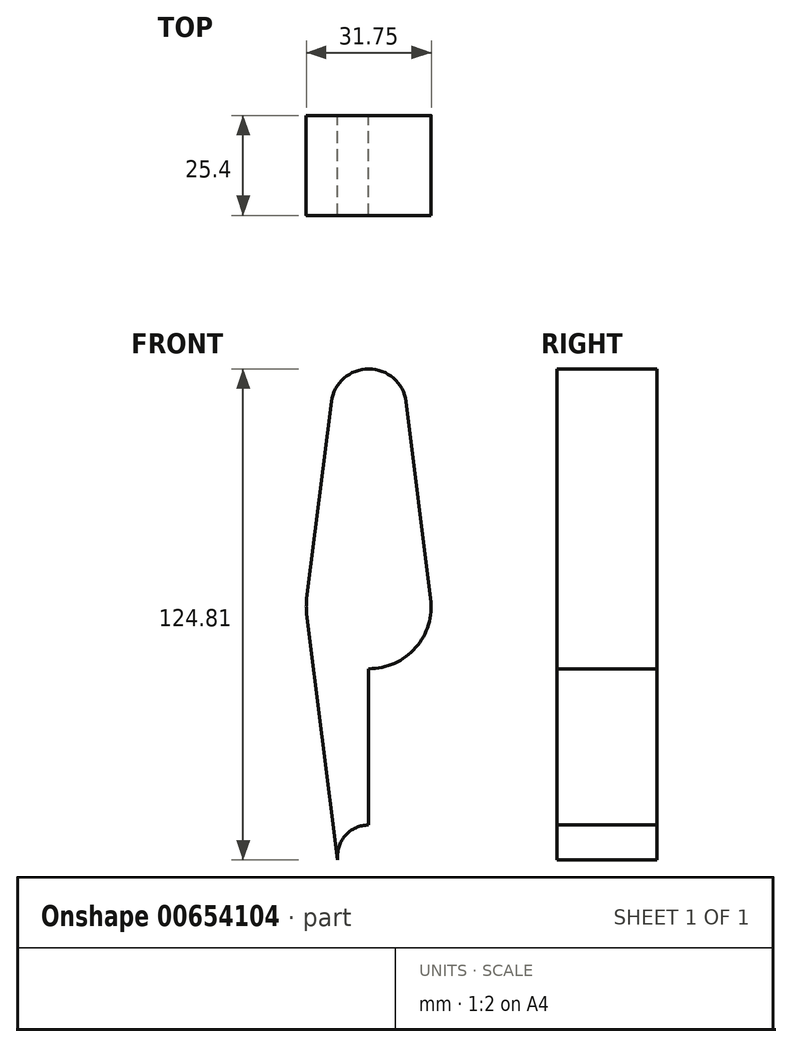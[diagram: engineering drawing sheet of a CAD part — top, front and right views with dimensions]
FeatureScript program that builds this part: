
annotation { "Feature Type Name" : "Feature", "Feature Type Description" : "" }
export const myFeature = defineFeature(function(context is Context, id is Id, definition is map)
    precondition{}
    {
        {
            var Q0;
            Q0=qCreatedBy(makeId("Front.planeOp"),FACE);
            var sketch = newSketch(context, id + "F0", { "sketchPlane" : qUnion([Q0])});
            skLineSegment(sketch, "E0", {"start": v(-10.04, 50.8) * mm, "end": v(-10.04, -63.5) * mm});
            skLineSegment(sketch, "E1", {"start": v(-10.04, -63.5) * mm, "end": v(34.41, -63.5) * mm});
            skCircle(sketch, "E2", {"center": v(-10.04, 50.8) * mm, "radius": 9.53 * mm});
            skCircle(sketch, "E3", {"center": v(-10.04, 0) * mm, "radius": 15.88 * mm});
            skPoint(sketch, "E3.centerSnap0", {"position": v(-10.04, -6.35) * mm});
            skCircle(sketch, "E4", {"center": v(-10.04, -63.5) * mm, "radius": 7.94 * mm});
            skCircle(sketch, "E5", {"center": v(34.41, -63.5) * mm, "radius": 7.94 * mm});
            skLineSegment(sketch, "E6", {"start": v(-19.49, 52) * mm, "end": v(-26.04, 0) * mm});
            skLineSegment(sketch, "E7", {"start": v(-26.04, 0) * mm, "end": v(-17.91, -64.5) * mm});
            skLineSegment(sketch, "E8", {"start": v(-0.59, 52) * mm, "end": v(5.96, 0) * mm});
            skLineSegment(sketch, "E9", {"start": v(5.96, 0) * mm, "end": v(0.89, -40.3) * mm});
            skLineSegment(sketch, "E10", {"start": v(6.91, -48.95) * mm, "end": v(34.41, -55.35) * mm});
            skLineSegment(sketch, "E11", {"start": v(-10.07, -71.44) * mm, "end": v(34.41, -71.44) * mm});
            skPoint(sketch, "E12.visualSharp", {"position": v(0, -47.34) * mm});
            skArc(sketch, "E12.filletArc", {"start": v(0.89, -40.3) * mm, "mid": v(2.24, -45.78) * mm, "end": v(6.91, -48.95) * mm});
            skSolve(sketch);
        }
        {
            var Q0;
            {var subQ0=sQuery(id+"F0.wireOp",EDGE,"E2");var subQ1=sQuery(id+"F0.wireOp",EDGE,"E0");var subQ2=makeQuery(id+"F0.imprint","INTERSECT",VERTEX,{"derivedFrom":[subQ1,subQ0]});Q0=makeQuery(id+"F0.imprint","IMPRINT",FACE,{"disambiguationData":[TD([[makeQuery(id+"F0.imprint","IMPRINT",EDGE,{"disambiguationData":[TD([[subQ2,-1.0]])],"derivedFrom":subQ1}),-1.0]])]});}
            var Q1;
            {var subQ0=sQuery(id+"F0.wireOp",EDGE,"E2");var subQ1=sQuery(id+"F0.wireOp",EDGE,"E0");var subQ2=makeQuery(id+"F0.imprint","INTERSECT",VERTEX,{"derivedFrom":[subQ1,subQ0]});Q1=makeQuery(id+"F0.imprint","IMPRINT",FACE,{"disambiguationData":[TD([[makeQuery(id+"F0.imprint","IMPRINT",EDGE,{"disambiguationData":[TD([[subQ2,-1.0]])],"derivedFrom":subQ1}),1.0]])]});}
            var Q2;
            {var subQ0=sQuery(id+"F0.wireOp",EDGE,"E3");var subQ1=sQuery(id+"F0.wireOp",EDGE,"E0");var subQ2=makeQuery(id+"F0.imprint","INTERSECT",VERTEX,{"disambiguationData":[OD(0.0)],"derivedFrom":[subQ1,subQ0]});Q2=makeQuery(id+"F0.imprint","IMPRINT",FACE,{"disambiguationData":[TD([[makeQuery(id+"F0.imprint","IMPRINT",EDGE,{"disambiguationData":[TD([[subQ2,1.0]])],"derivedFrom":subQ1}),-1.0]])]});}
            var Q3;
            {var subQ0=sQuery(id+"F0.wireOp",EDGE,"E3");var subQ1=sQuery(id+"F0.wireOp",EDGE,"E0");var subQ2=makeQuery(id+"F0.imprint","INTERSECT",VERTEX,{"disambiguationData":[OD(0.0)],"derivedFrom":[subQ1,subQ0]});Q3=makeQuery(id+"F0.imprint","IMPRINT",FACE,{"disambiguationData":[TD([[makeQuery(id+"F0.imprint","IMPRINT",EDGE,{"disambiguationData":[TD([[subQ2,1.0]])],"derivedFrom":subQ1}),1.0]])]});}
            var Q4;
            {var subQ0=sQuery(id+"F0.wireOp",EDGE,"E3");var subQ1=sQuery(id+"F0.wireOp",EDGE,"E0");var subQ2=makeQuery(id+"F0.imprint","INTERSECT",VERTEX,{"disambiguationData":[OD(0.0)],"derivedFrom":[subQ1,subQ0]});Q4=makeQuery(id+"F0.imprint","IMPRINT",FACE,{"disambiguationData":[TD([[makeQuery(id+"F0.imprint","IMPRINT",EDGE,{"disambiguationData":[TD([[subQ2,-1.0]])],"derivedFrom":subQ1}),-1.0]])]});}
            var Q5;
            {var subQ0=sQuery(id+"F0.wireOp",EDGE,"E2");var subQ1=makeQuery(id+"F0.imprint","INTERSECT",VERTEX,{"derivedFrom":[subQ0,sQuery(id+"F0.wireOp",EDGE,"E6")]});Q5=makeQuery(id+"F0.imprint","IMPRINT",FACE,{"disambiguationData":[TD([[makeQuery(id+"F0.imprint","IMPRINT",EDGE,{"disambiguationData":[TD([[subQ1,1.0]])],"derivedFrom":subQ0}),1.0]])]});}
            extrude(context, id + "F1", {"entities" : qUnion([Q0, Q1, Q2, Q3, Q4, Q5]), "depth" : 25.4 * mm, "offsetDistance" : 25.4 * mm});
        }
    });
